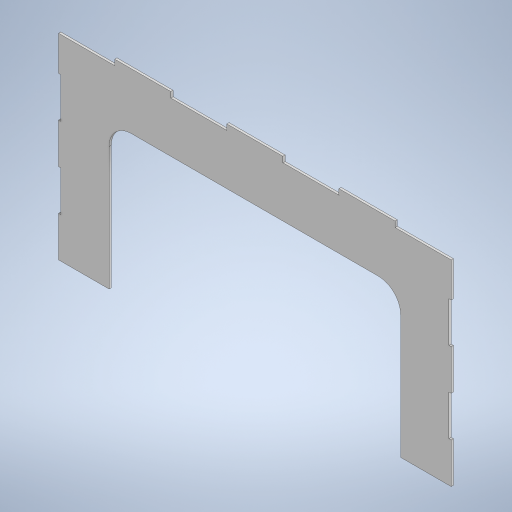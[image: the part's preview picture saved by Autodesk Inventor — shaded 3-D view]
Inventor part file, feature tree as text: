
AUTODESK INVENTOR PART (.ipt)
format: ipt  version: 2023 (Build 270158000, 158)  size: 291,328 bytes
history: native  units: mm
features: extrude x3, sketch x3
ambient origin geometry x8: Origin, YZ Plane, XZ Plane, XY Plane, X Axis, Y Axis, Z Axis, Center Point
bodies: Solid1 (feature_tree)
feature tree (6):
  extrude  "Extrusion1"  Depth=180.0mm
  extrude  "Extrusion2"  Depth=45.0mm
  extrude  "Extrusion3"  Depth=20.0mm
  sketch  "Sketch1"  dims[d0=350.0mm d1=180.0mm]
  sketch  "Sketch2"  dims[d2=45.0mm d3=45.0mm]
  sketch  "Sketch3"  dims[d4=50.0mm d5=20.0mm d6=2.0mm d7=0.0mm d8=50.0mm d9=50.0mm d10=50.0mm d11=50.0mm d12=50.0mm d13=50.0mm d14=50.0mm d15=5.0mm d16=2.0mm d17=0.0mm d26=2.0mm d27=0.0mm d28=36.0mm d29=2.0mm d30=2.0mm d31=36.0mm d32=36.0mm d33=36.0mm d34=2.0mm d35=36.0mm d36=36.0mm d37=36.0mm d38=36.0mm]
